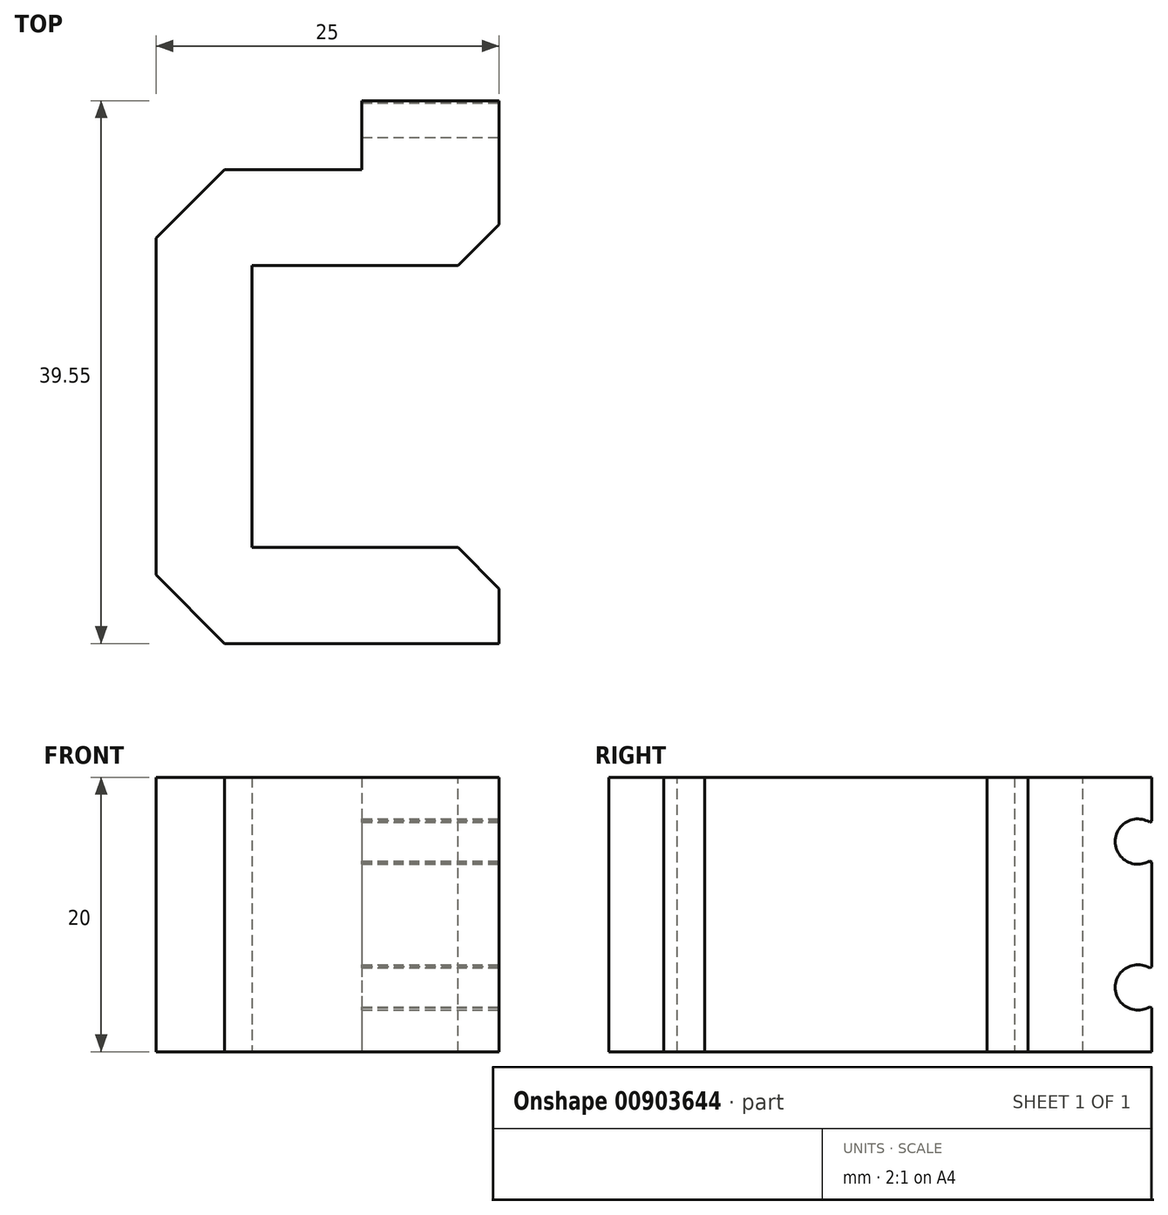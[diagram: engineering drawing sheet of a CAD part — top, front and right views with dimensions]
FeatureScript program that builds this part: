
annotation { "Feature Type Name" : "Feature", "Feature Type Description" : "" }
export const myFeature = defineFeature(function(context is Context, id is Id, definition is map)
    precondition{}
    {
        {
            var Q0;
            Q0=qCreatedBy(makeId("Top.planeOp"),FACE);
            var sketch = newSketch(context, id + "F0", { "sketchPlane" : qUnion([Q0])});
            skLineSegment(sketch, "E0.left", {"start": v(-14, 17.28) * mm, "end": v(-14, -17.28) * mm});
            skLineSegment(sketch, "E0.right", {"start": v(-7, 10.28) * mm, "end": v(-7, -10.28) * mm});
            skPoint(sketch, "E0.middle", {"position": v(0, 0) * mm});
            skLineSegment(sketch, "E1.top", {"start": v(-7, 10.27) * mm, "end": v(11, 10.28) * mm});
            skLineSegment(sketch, "E1.right", {"start": v(11, 17.28) * mm, "end": v(11, 10.27) * mm});
            skPoint(sketch, "E1.middle", {"position": v(2, 13.78) * mm});
            skLineSegment(sketch, "E2.top", {"start": v(-7, -10.28) * mm, "end": v(11, -10.27) * mm});
            skLineSegment(sketch, "E2.right", {"start": v(11, -17.28) * mm, "end": v(11, -10.27) * mm});
            skPoint(sketch, "E2.middle", {"position": v(2, -13.78) * mm});
            skLineSegment(sketch, "E3", {"start": v(-14, 17.28) * mm, "end": v(11, 17.28) * mm});
            skLineSegment(sketch, "E4", {"start": v(-14, -17.28) * mm, "end": v(11, -17.28) * mm});
            skLineSegment(sketch, "E5", {"start": v(-7, 0) * mm, "end": v(0, 0) * mm, "construction": true});
            skSolve(sketch);
        }
        {
            var Q0;
            Q0=makeQuery(id+"F0.imprint","IMPRINT",FACE,{"disambiguationData":[TD([[makeQuery(id+"F0.imprint","IMPRINT",EDGE,{"derivedFrom":sQuery(id+"F0.wireOp",EDGE,"E0.left")}),1.0]])]});
            extrude(context, id + "F1", {"entities" : qUnion([Q0]), "depth" : 20 * mm, "offsetDistance" : 25 * mm});
        }
        {
            var Q0;
            Q0=makeQuery(id+"F1.opExtrude","SWEPT_FACE",FACE,{"disambiguationData":[OSD([sQuery(id+"F0.wireOp",EDGE,"E1.right")])]});
            var sketch = newSketch(context, id + "F2", { "sketchPlane" : qUnion([Q0])});
            skArc(sketch, "E6", {"start": v(22.27, 16.62) * mm, "mid": v(19.63, 15.31) * mm, "end": v(22.27, 14) * mm});
            skLineSegment(sketch, "E7", {"start": v(17.28, 20) * mm, "end": v(22.28, 20) * mm});
            skLineSegment(sketch, "E8", {"start": v(22.28, 20) * mm, "end": v(22.28, 16.62) * mm});
            skLineSegment(sketch, "E9", {"start": v(22.28, 14) * mm, "end": v(22.28, 6) * mm});
            skArc(sketch, "E10", {"start": v(22.27, 6) * mm, "mid": v(19.63, 4.69) * mm, "end": v(22.27, 3.38) * mm});
            skLineSegment(sketch, "E11", {"start": v(22.28, 3.38) * mm, "end": v(22.28, 0) * mm});
            skLineSegment(sketch, "E12", {"start": v(22.28, 0) * mm, "end": v(17.28, 0) * mm});
            skSolve(sketch);
        }
        {
            var Q0;
            Q0=makeQuery(id+"F2.imprint","IMPRINT",FACE,{"disambiguationData":[TD([[makeQuery(id+"F2.imprint","IMPRINT",EDGE,{"derivedFrom":sQuery(id+"F2.wireOp",EDGE,"E6")}),-1.0]])]});
            var Q1;
            Q1=makeQuery(id+"F1.opExtrude","SWEPT_FACE",FACE,{"disambiguationData":[OSD([sQuery(id+"F0.wireOp",EDGE,"E0.left")])]});
            extrude(context, id + "F3", {"entities" : qUnion([Q0]), "operationType" : NewBodyOperationType.ADD, "oppositeDirection" : true, "depth" : 10 * mm, "endBoundEntityFace" : qUnion([Q1]), "offsetDistance" : 25 * mm});
        }
        {
            var Q0;
            Q0=makeQuery(id+"F1.opExtrude","SWEPT_EDGE",EDGE,{"disambiguationData":[OSD([sQuery(id+"F0.wireOp",EDGE,"E1.top"),sQuery(id+"F0.wireOp",EDGE,"E1.right")])]});
            var Q1;
            Q1=makeQuery(id+"F1.opExtrude","SWEPT_EDGE",EDGE,{"disambiguationData":[OSD([sQuery(id+"F0.wireOp",EDGE,"E2.top"),sQuery(id+"F0.wireOp",EDGE,"E2.right")])]});
            chamfer(context, id + "F4", {"entities" : qUnion([Q0, Q1]), "width" : 3 * mm, "tangentPropagation" : true});
        }
        {
            var Q0;
            Q0=makeQuery(id+"F3.opExtrude","SWEPT_EDGE",EDGE,{"disambiguationData":[OSD([sQuery(id+"F2.wireOp",EDGE,"E6"),sQuery(id+"F2.wireOp",EDGE,"E8")])]});
            var Q1;
            Q1=makeQuery(id+"F3.opExtrude","SWEPT_EDGE",EDGE,{"disambiguationData":[OSD([sQuery(id+"F2.wireOp",EDGE,"E6"),sQuery(id+"F2.wireOp",EDGE,"E9")])]});
            var Q2;
            Q2=makeQuery(id+"F3.opExtrude","SWEPT_EDGE",EDGE,{"disambiguationData":[OSD([sQuery(id+"F2.wireOp",EDGE,"E9"),sQuery(id+"F2.wireOp",EDGE,"E10")])]});
            var Q3;
            Q3=makeQuery(id+"F3.opExtrude","SWEPT_EDGE",EDGE,{"disambiguationData":[OSD([sQuery(id+"F2.wireOp",EDGE,"E10"),sQuery(id+"F2.wireOp",EDGE,"E11")])]});
            chamfer(context, id + "F5", {"entities" : qUnion([Q0, Q1, Q2, Q3]), "width" : 0.1 * mm, "tangentPropagation" : true});
        }
        {
            var Q0;
            Q0=makeQuery(id+"F1.opExtrude","SWEPT_EDGE",EDGE,{"disambiguationData":[OSD([sQuery(id+"F0.wireOp",EDGE,"E0.left"),sQuery(id+"F0.wireOp",EDGE,"E3")])]});
            var Q1;
            Q1=makeQuery(id+"F1.opExtrude","SWEPT_EDGE",EDGE,{"disambiguationData":[OSD([sQuery(id+"F0.wireOp",EDGE,"E0.left"),sQuery(id+"F0.wireOp",EDGE,"E4")])]});
            chamfer(context, id + "F6", {"entities" : qUnion([Q0, Q1]), "width" : 5 * mm, "tangentPropagation" : true});
        }
    });
